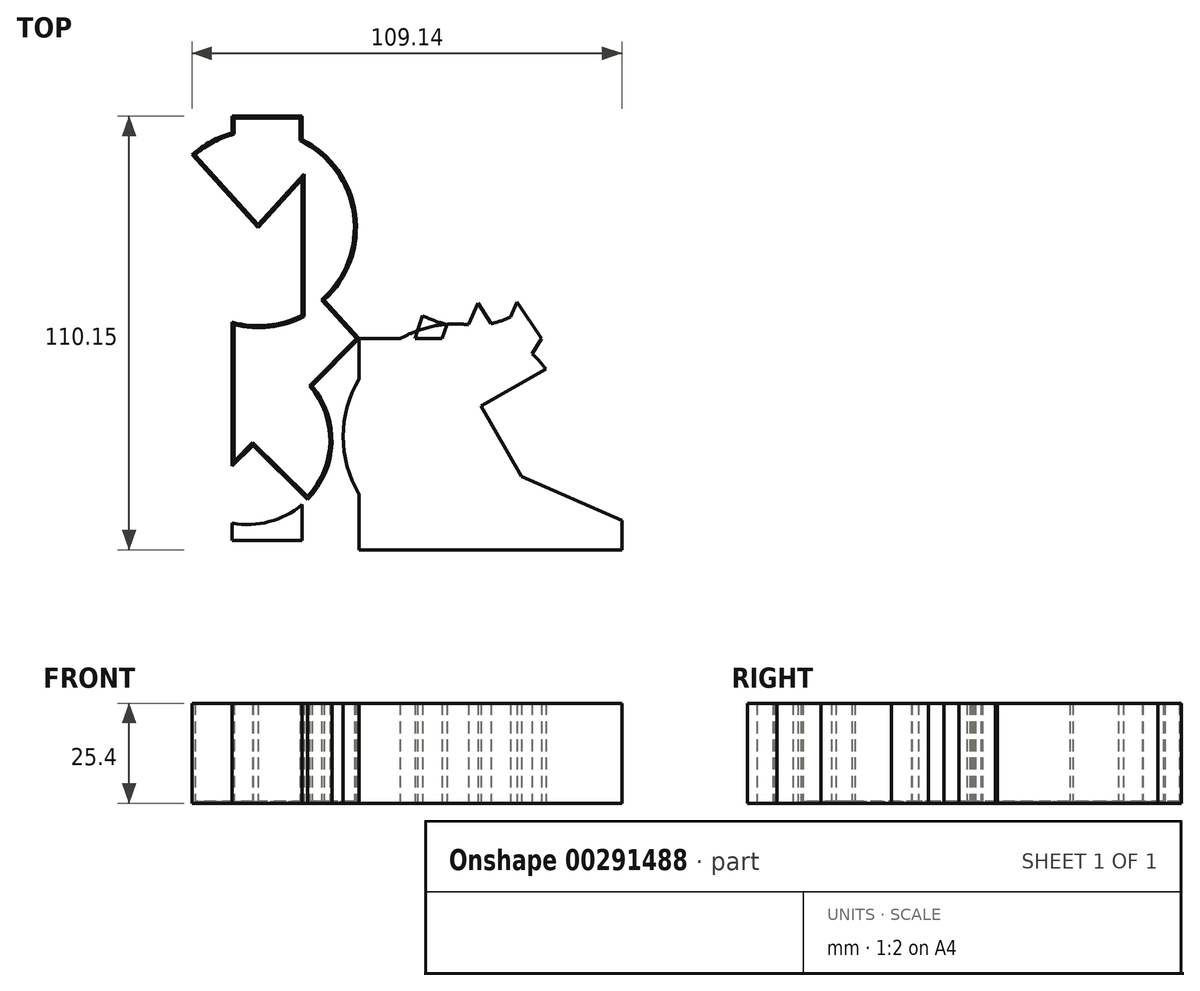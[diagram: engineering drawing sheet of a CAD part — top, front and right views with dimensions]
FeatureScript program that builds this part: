
annotation { "Feature Type Name" : "Feature", "Feature Type Description" : "" }
export const myFeature = defineFeature(function(context is Context, id is Id, definition is map)
    precondition{}
    {
        {
            var Q0;
            Q0=qCreatedBy(makeId("Top.planeOp"),FACE);
            var sketch = newSketch(context, id + "F0", { "sketchPlane" : qUnion([Q0])});
            skLineSegment(sketch, "E0.bottom", {"start": v(-41.08, 59.73) * mm, "end": v(-23.36, 59.73) * mm});
            skLineSegment(sketch, "E0.left", {"start": v(-60.14, 3.2) * mm, "end": v(-60.14, 0) * mm});
            skLineSegment(sketch, "E0.right", {"start": v(-8.86, 4.62) * mm, "end": v(-8.86, 3.2) * mm});
            skLineSegment(sketch, "E1.top", {"start": v(-60.14, 3.2) * mm, "end": v(-23.36, 3.2) * mm});
            skLineSegment(sketch, "E2", {"start": v(27.12, 3.2) * mm, "end": v(27.12, 3.2) * mm});
            skLineSegment(sketch, "E3.top", {"start": v(-41.08, -48.07) * mm, "end": v(-23.36, -48.07) * mm});
            skLineSegment(sketch, "E3.left", {"start": v(-41.08, 59.73) * mm, "end": v(-41.08, 55.54) * mm});
            skLineSegment(sketch, "E3.right", {"start": v(-23.36, 59.73) * mm, "end": v(-23.36, -48.07) * mm});
            skLineSegment(sketch, "E4", {"start": v(-51.27, 49.95) * mm, "end": v(-34.5, 31.47) * mm});
            skPoint(sketch, "E4.endSnap0", {"position": v(-8.86, 4.62) * mm});
            skLineSegment(sketch, "E5", {"start": v(-8.86, 3.2) * mm, "end": v(-23.36, -11.36) * mm});
            skLineSegment(sketch, "E6", {"start": v(-8.86, 59.73) * mm, "end": v(-34.5, 31.47) * mm});
            skArc(sketch, "E7", {"start": v(-51.27, 13) * mm, "mid": v(-9.55, 31.47) * mm, "end": v(-51.27, 49.95) * mm});
            skPoint(sketch, "E8.centerSnap0", {"position": v(-34.5, -25.24) * mm});
            skPoint(sketch, "E9.centerSnap0", {"position": v(-34.5, -22.56) * mm});
            skLineSegment(sketch, "E10.bottom", {"start": v(-8.86, 3.2) * mm, "end": v(17.29, 3.2) * mm});
            skLineSegment(sketch, "E10.top", {"start": v(-8.86, -50.42) * mm, "end": v(57.87, -50.42) * mm});
            skLineSegment(sketch, "E10.left", {"start": v(-8.86, 3.2) * mm, "end": v(-8.86, -50.42) * mm});
            skLineSegment(sketch, "E10.right", {"start": v(57.87, -43.02) * mm, "end": v(57.87, -50.42) * mm});
            skArc(sketch, "E11", {"start": v(5.39, -48.37) * mm, "mid": v(12.64, -50.13) * mm, "end": v(20.1, -49.96) * mm});
            skLineSegment(sketch, "E12", {"start": v(22.08, -13.94) * mm, "end": v(43.06, -50.42) * mm});
            skLineSegment(sketch, "E13", {"start": v(37.5, 3.2) * mm, "end": v(29.47, -9.69) * mm});
            skLineSegment(sketch, "E14", {"start": v(-11.46, -12.65) * mm, "end": v(-8.86, -13.79) * mm});
            skLineSegment(sketch, "E15", {"start": v(42.4, 0) * mm, "end": v(44.2, -18.96) * mm});
            skLineSegment(sketch, "E16", {"start": v(51.9, 3.2) * mm, "end": v(22.08, -13.94) * mm});
            skLineSegment(sketch, "E17", {"start": v(11.77, -19.86) * mm, "end": v(20.1, -49.96) * mm});
            skLineSegment(sketch, "E18.trimOffspring", {"start": v(13.5, 6.86) * mm, "end": v(12.22, 3.2) * mm});
            skLineSegment(sketch, "E19.trimOffspring", {"start": v(7.23, 9.08) * mm, "end": v(5.39, 3.2) * mm});
            skLineSegment(sketch, "E20.trimOffspring", {"start": v(-34.5, -22.56) * mm, "end": v(-41.08, -29.17) * mm});
            skLineSegment(sketch, "E21.trimOffspring", {"start": v(27.12, 3.2) * mm, "end": v(56.48, 3.2) * mm});
            skLineSegment(sketch, "E22.trimOffspring", {"start": v(-23.36, 19.19) * mm, "end": v(-8.86, 3.2) * mm});
            skArc(sketch, "E23.trimOffspring", {"start": v(27.63, 4.35) * mm, "mid": v(14.46, 6.92) * mm, "end": v(1.56, 3.2) * mm});
            skLineSegment(sketch, "E24.trimOffspring", {"start": v(-41.08, 38.72) * mm, "end": v(-41.08, -48.07) * mm});
            skLineSegment(sketch, "E25.trimOffspring", {"start": v(8.85, -21.54) * mm, "end": v(57.87, -43.02) * mm});
            skLineSegment(sketch, "E26.trimOffspring", {"start": v(19.25, -26.1) * mm, "end": v(5.39, -48.37) * mm});
            skArc(sketch, "E27.trimOffspring", {"start": v(38.57, -4.45) * mm, "mid": v(34.6, -0.18) * mm, "end": v(29.85, 3.2) * mm});
            skPoint(sketch, "E28.orphan", {"position": v(17.29, 3.2) * mm});
            skLineSegment(sketch, "E29.trimOffspring", {"start": v(25.47, 21.33) * mm, "end": v(18.68, 6.3) * mm});
            skLineSegment(sketch, "E30.trimOffspring", {"start": v(-8.86, 3.2) * mm, "end": v(12.22, 3.2) * mm});
            skLineSegment(sketch, "E31.trimOffspring", {"start": v(-51.27, 13) * mm, "end": v(-60.14, 3.2) * mm});
            skArc(sketch, "E32.trimOffspring", {"start": v(7.23, 9.08) * mm, "mid": v(20.14, 6.33) * mm, "end": v(32.67, 10.49) * mm});
            skPoint(sketch, "E33.orphan", {"position": v(-60.14, -48.33) * mm});
            skArc(sketch, "E34.trimOffspring", {"start": v(-41.08, -43.67) * mm, "mid": v(-17.83, -31.73) * mm, "end": v(-23.36, -6.2) * mm});
            skLineSegment(sketch, "E35.trimOffspring", {"start": v(-8.86, -6.98) * mm, "end": v(-8.86, -50.49) * mm});
            skArc(sketch, "E36.trimOffspring", {"start": v(-8.86, -6.98) * mm, "mid": v(-12.92, -21.67) * mm, "end": v(-8.86, -36.36) * mm});
            skLineSegment(sketch, "E37.trimOffspring", {"start": v(21.37, 12.25) * mm, "end": v(27.12, 3.2) * mm});
            skLineSegment(sketch, "E38.trimOffspring", {"start": v(-41.08, -18.77) * mm, "end": v(-8.86, -50.49) * mm});
            skLineSegment(sketch, "E39.trimOffspring", {"start": v(11.77, -19.86) * mm, "end": v(-8.86, -31.73) * mm});
            skLineSegment(sketch, "E40.trimOffspring", {"start": v(31.32, 12.51) * mm, "end": v(27.12, 3.2) * mm});
            skPoint(sketch, "E41.trimOffspring.end.orphan", {"position": v(0, 59.73) * mm});
            skLineSegment(sketch, "E42.trimOffspring", {"start": v(31.32, 12.51) * mm, "end": v(37.5, 3.2) * mm});
            skLineSegment(sketch, "E43.trimOffspring", {"start": v(27.12, 3.2) * mm, "end": v(57.87, 3.2) * mm});
            skLineSegment(sketch, "E44.trimOffspring", {"start": v(46, -37.82) * mm, "end": v(47.2, -50.42) * mm});
            skArc(sketch, "E45.trimOffspring", {"start": v(37.32, -40.44) * mm, "mid": v(39.17, -38.07) * mm, "end": v(40.76, -35.52) * mm});
            skSolve(sketch);
        }
        {
            var Q0;
            {var subQ1=sQuery(id+"F0.wireOp",EDGE,"E11");Q0=makeQuery(id+"F0.imprint","IMPRINT",FACE,{"disambiguationData":[TD([[makeQuery(id+"F0.imprint","IMPRINT",EDGE,{"derivedFrom":subQ1}),-1.0]])]});}
            var Q1;
            {var subQ0=sQuery(id+"F0.wireOp",EDGE,"E22.trimOffspring");var subQ1=sQuery(id+"F0.wireOp",EDGE,"E3.right");var subQ2=makeQuery(id+"F0.imprint","INTERSECT",VERTEX,{"derivedFrom":[subQ1,subQ0]});Q1=makeQuery(id+"F0.imprint","IMPRINT",FACE,{"disambiguationData":[TD([[makeQuery(id+"F0.imprint","IMPRINT",EDGE,{"disambiguationData":[TD([[subQ2,-1.0]])],"derivedFrom":subQ1}),1.0]])]});}
            var Q2;
            {var subQ0=sQuery(id+"F0.wireOp",EDGE,"E22.trimOffspring");var subQ1=sQuery(id+"F0.wireOp",EDGE,"E3.right");var subQ2=makeQuery(id+"F0.imprint","INTERSECT",VERTEX,{"derivedFrom":[subQ1,subQ0]});Q2=makeQuery(id+"F0.imprint","IMPRINT",FACE,{"disambiguationData":[TD([[makeQuery(id+"F0.imprint","IMPRINT",EDGE,{"disambiguationData":[TD([[subQ2,1.0]])],"derivedFrom":subQ1}),1.0]])]});}
            var Q3;
            {var subQ3=sQuery(id+"F0.wireOp",EDGE,"E3.right");var subQ5=sQuery(id+"F0.wireOp",EDGE,"E7");var subQ9=makeQuery(id+"F0.imprint","INTERSECT",VERTEX,{"disambiguationData":[OD(0.0)],"derivedFrom":[subQ3,subQ5]});Q3=makeQuery(id+"F0.imprint","IMPRINT",FACE,{"disambiguationData":[TD([[makeQuery(id+"F0.imprint","IMPRINT",EDGE,{"disambiguationData":[TD([[subQ9,-1.0]])],"derivedFrom":subQ3}),-1.0]])]});}
            var Q4;
            {var subQ3=sQuery(id+"F0.wireOp",EDGE,"E3.right");var subQ9=makeQuery(id+"F0.imprint","INTERSECT",VERTEX,{"derivedFrom":[sQuery(id+"F0.wireOp",EDGE,"E1.top"),subQ3]});Q4=makeQuery(id+"F0.imprint","IMPRINT",FACE,{"disambiguationData":[TD([[makeQuery(id+"F0.imprint","IMPRINT",EDGE,{"disambiguationData":[TD([[subQ9,1.0]])],"derivedFrom":subQ3}),1.0]])]});}
            var Q5;
            {var subQ15=sQuery(id+"F0.wireOp",EDGE,"E10.left");Q5=makeQuery(id+"F0.imprint","IMPRINT",FACE,{"disambiguationData":[TD([[makeQuery(id+"F0.imprint","IMPRINT",EDGE,{"derivedFrom":subQ15}),1.0]])]});}
            var Q6;
            {var subQ0=sQuery(id+"F0.wireOp",EDGE,"E44.trimOffspring");Q6=makeQuery(id+"F0.imprint","IMPRINT",FACE,{"disambiguationData":[TD([[makeQuery(id+"F0.imprint","IMPRINT",EDGE,{"derivedFrom":subQ0}),-1.0]])]});}
            var Q7;
            {var subQ0=sQuery(id+"F0.wireOp",EDGE,"E26.trimOffspring");var subQ1=sQuery(id+"F0.wireOp",EDGE,"E17");var subQ2=makeQuery(id+"F0.imprint","INTERSECT",VERTEX,{"derivedFrom":[subQ1,subQ0]});Q7=makeQuery(id+"F0.imprint","IMPRINT",FACE,{"disambiguationData":[TD([[makeQuery(id+"F0.imprint","IMPRINT",EDGE,{"disambiguationData":[TD([[subQ2,1.0]])],"derivedFrom":subQ1}),1.0]])]});}
            var Q8;
            {var subQ0=sQuery(id+"F0.wireOp",EDGE,"E24.trimOffspring");var subQ1=sQuery(id+"F0.wireOp",EDGE,"E20.trimOffspring");var subQ2=makeQuery(id+"F0.imprint","INTERSECT",VERTEX,{"derivedFrom":[subQ1,subQ0]});Q8=makeQuery(id+"F0.imprint","IMPRINT",FACE,{"disambiguationData":[TD([[makeQuery(id+"F0.imprint","IMPRINT",EDGE,{"disambiguationData":[TD([[subQ2,1.0]])],"derivedFrom":subQ1}),-1.0]])]});}
            var Q9;
            {var subQ0=sQuery(id+"F0.wireOp",EDGE,"E5");var subQ1=sQuery(id+"F0.wireOp",EDGE,"E3.right");var subQ2=makeQuery(id+"F0.imprint","INTERSECT",VERTEX,{"derivedFrom":[subQ1,subQ0]});Q9=makeQuery(id+"F0.imprint","IMPRINT",FACE,{"disambiguationData":[TD([[makeQuery(id+"F0.imprint","IMPRINT",EDGE,{"disambiguationData":[TD([[subQ2,-1.0]])],"derivedFrom":subQ1}),1.0]])]});}
            var Q10;
            {var subQ0=sQuery(id+"F0.wireOp",EDGE,"E14");Q10=makeQuery(id+"F0.imprint","IMPRINT",FACE,{"disambiguationData":[TD([[makeQuery(id+"F0.imprint","IMPRINT",EDGE,{"derivedFrom":subQ0}),-1.0]])]});}
            var Q11;
            {var subQ0=sQuery(id+"F0.wireOp",EDGE,"E0.bottom");Q11=makeQuery(id+"F0.imprint","IMPRINT",FACE,{"disambiguationData":[TD([[makeQuery(id+"F0.imprint","IMPRINT",EDGE,{"derivedFrom":subQ0}),-1.0]])]});}
            var Q12;
            {var subQ0=sQuery(id+"F0.wireOp",EDGE,"E40.trimOffspring");var subQ1=sQuery(id+"F0.wireOp",EDGE,"E23.trimOffspring");var subQ2=makeQuery(id+"F0.imprint","INTERSECT",VERTEX,{"derivedFrom":[subQ1,subQ0]});Q12=makeQuery(id+"F0.imprint","IMPRINT",FACE,{"disambiguationData":[TD([[makeQuery(id+"F0.imprint","IMPRINT",EDGE,{"disambiguationData":[TD([[subQ2,-1.0]])],"derivedFrom":subQ1}),-1.0]])]});}
            var Q13;
            {var subQ0=sQuery(id+"F0.wireOp",EDGE,"E3.top");Q13=makeQuery(id+"F0.imprint","IMPRINT",FACE,{"disambiguationData":[TD([[makeQuery(id+"F0.imprint","IMPRINT",EDGE,{"derivedFrom":subQ0}),1.0]])]});}
            var Q14;
            {var subQ0=sQuery(id+"F0.wireOp",EDGE,"E10.right");Q14=makeQuery(id+"F0.imprint","IMPRINT",FACE,{"disambiguationData":[TD([[makeQuery(id+"F0.imprint","IMPRINT",EDGE,{"derivedFrom":subQ0}),-1.0]])]});}
            var Q15;
            {var subQ0=sQuery(id+"F0.wireOp",EDGE,"E11");Q15=makeQuery(id+"F0.imprint","IMPRINT",FACE,{"disambiguationData":[TD([[makeQuery(id+"F0.imprint","IMPRINT",EDGE,{"derivedFrom":subQ0}),1.0]])]});}
            var Q16;
            {var subQ0=sQuery(id+"F0.wireOp",EDGE,"E5");var subQ1=sQuery(id+"F0.wireOp",EDGE,"E3.right");var subQ2=makeQuery(id+"F0.imprint","INTERSECT",VERTEX,{"derivedFrom":[subQ1,subQ0]});Q16=makeQuery(id+"F0.imprint","IMPRINT",FACE,{"disambiguationData":[TD([[makeQuery(id+"F0.imprint","IMPRINT",EDGE,{"disambiguationData":[TD([[subQ2,1.0]])],"derivedFrom":subQ1}),1.0]])]});}
            var Q17;
            {var subQ4=sQuery(id+"F0.wireOp",EDGE,"E32.trimOffspring");var subQ6=sQuery(id+"F0.wireOp",EDGE,"E42.trimOffspring");var subQ7=makeQuery(id+"F0.imprint","INTERSECT",VERTEX,{"derivedFrom":[subQ4,subQ6]});Q17=makeQuery(id+"F0.imprint","IMPRINT",FACE,{"disambiguationData":[TD([[makeQuery(id+"F0.imprint","IMPRINT",EDGE,{"disambiguationData":[TD([[subQ7,1.0]])],"derivedFrom":subQ4}),-1.0]])]});}
            var Q18;
            {var subQ0=sQuery(id+"F0.wireOp",EDGE,"E32.trimOffspring");var subQ1=sQuery(id+"F0.wireOp",EDGE,"E19.trimOffspring");var subQ2=makeQuery(id+"F0.imprint","INTERSECT",VERTEX,{"derivedFrom":[subQ1,subQ0]});Q18=makeQuery(id+"F0.imprint","IMPRINT",FACE,{"disambiguationData":[TD([[makeQuery(id+"F0.imprint","IMPRINT",EDGE,{"disambiguationData":[TD([[subQ2,-1.0]])],"derivedFrom":subQ1}),1.0]])]});}
            var Q19;
            {var subQ0=sQuery(id+"F0.wireOp",EDGE,"E3.right");var subQ1=sQuery(id+"F0.wireOp",EDGE,"E1.top");var subQ2=makeQuery(id+"F0.imprint","INTERSECT",VERTEX,{"derivedFrom":[subQ1,subQ0]});Q19=makeQuery(id+"F0.imprint","IMPRINT",FACE,{"disambiguationData":[TD([[makeQuery(id+"F0.imprint","IMPRINT",EDGE,{"disambiguationData":[TD([[subQ2,1.0]])],"derivedFrom":subQ1}),1.0]])]});}
            var Q20;
            {var subQ0=sQuery(id+"F0.wireOp",EDGE,"E7");var subQ1=sQuery(id+"F0.wireOp",EDGE,"E3.right");var subQ2=makeQuery(id+"F0.imprint","INTERSECT",VERTEX,{"disambiguationData":[OD(0.0)],"derivedFrom":[subQ1,subQ0]});Q20=makeQuery(id+"F0.imprint","IMPRINT",FACE,{"disambiguationData":[TD([[makeQuery(id+"F0.imprint","IMPRINT",EDGE,{"disambiguationData":[TD([[subQ2,-1.0]])],"derivedFrom":subQ1}),1.0]])]});}
            var Q21;
            {var subQ0=sQuery(id+"F0.wireOp",EDGE,"E45.trimOffspring");Q21=makeQuery(id+"F0.imprint","IMPRINT",FACE,{"disambiguationData":[TD([[makeQuery(id+"F0.imprint","IMPRINT",EDGE,{"derivedFrom":subQ0}),1.0]])]});}
            var Q22;
            {var subQ0=sQuery(id+"F0.wireOp",EDGE,"E43.trimOffspring");var subQ5=sQuery(id+"F0.wireOp",EDGE,"E16");var subQ6=makeQuery(id+"F0.imprint","INTERSECT",VERTEX,{"derivedFrom":[subQ5,subQ0]});Q22=makeQuery(id+"F0.imprint","IMPRINT",FACE,{"disambiguationData":[TD([[makeQuery(id+"F0.imprint","IMPRINT",EDGE,{"disambiguationData":[TD([[subQ6,-1.0]])],"derivedFrom":subQ5}),-1.0]])]});}
            var Q23;
            {var subQ0=sQuery(id+"F0.wireOp",EDGE,"E16");var subQ1=sQuery(id+"F0.wireOp",EDGE,"E13");var subQ2=makeQuery(id+"F0.imprint","INTERSECT",VERTEX,{"derivedFrom":[subQ1,subQ0]});Q23=makeQuery(id+"F0.imprint","IMPRINT",FACE,{"disambiguationData":[TD([[makeQuery(id+"F0.imprint","IMPRINT",EDGE,{"disambiguationData":[TD([[subQ2,1.0]])],"derivedFrom":subQ1}),1.0]])]});}
            var Q24;
            {var subQ9=sQuery(id+"F0.wireOp",EDGE,"E10.left");Q24=makeQuery(id+"F0.imprint","IMPRINT",FACE,{"disambiguationData":[TD([[makeQuery(id+"F0.imprint","IMPRINT",EDGE,{"derivedFrom":subQ9}),-1.0]])]});}
            var Q25;
            {var subQ0=sQuery(id+"F0.wireOp",EDGE,"E43.trimOffspring");var subQ3=sQuery(id+"F0.wireOp",EDGE,"E27.trimOffspring");var subQ5=makeQuery(id+"F0.imprint","INTERSECT",VERTEX,{"derivedFrom":[subQ3,subQ0]});Q25=makeQuery(id+"F0.imprint","IMPRINT",FACE,{"disambiguationData":[TD([[makeQuery(id+"F0.imprint","IMPRINT",EDGE,{"disambiguationData":[TD([[subQ5,1.0]])],"derivedFrom":subQ3}),-1.0]])]});}
            var Q26;
            {var subQ0=sQuery(id+"F0.wireOp",EDGE,"E30.trimOffspring");var subQ1=sQuery(id+"F0.wireOp",EDGE,"E18.trimOffspring");var subQ2=makeQuery(id+"F0.imprint","INTERSECT",VERTEX,{"derivedFrom":[subQ1,subQ0]});Q26=makeQuery(id+"F0.imprint","IMPRINT",FACE,{"disambiguationData":[TD([[makeQuery(id+"F0.imprint","IMPRINT",EDGE,{"disambiguationData":[TD([[subQ2,1.0]])],"derivedFrom":subQ1}),-1.0]])]});}
            var Q27;
            {var subQ0=sQuery(id+"F0.wireOp",EDGE,"E29.trimOffspring");var subQ1=sQuery(id+"F0.wireOp",EDGE,"E23.trimOffspring");var subQ2=makeQuery(id+"F0.imprint","INTERSECT",VERTEX,{"derivedFrom":[subQ1,subQ0]});Q27=makeQuery(id+"F0.imprint","IMPRINT",FACE,{"disambiguationData":[TD([[makeQuery(id+"F0.imprint","IMPRINT",EDGE,{"disambiguationData":[TD([[subQ2,1.0]])],"derivedFrom":subQ1}),-1.0]])]});}
            var Q28;
            {var subQ0=sQuery(id+"F0.wireOp",EDGE,"E34.trimOffspring");var subQ3=sQuery(id+"F0.wireOp",EDGE,"E3.right");var subQ4=makeQuery(id+"F0.imprint","INTERSECT",VERTEX,{"disambiguationData":[OD(1.0)],"derivedFrom":[subQ3,subQ0]});Q28=makeQuery(id+"F0.imprint","IMPRINT",FACE,{"disambiguationData":[TD([[makeQuery(id+"F0.imprint","IMPRINT",EDGE,{"disambiguationData":[TD([[subQ4,1.0]])],"derivedFrom":subQ3}),-1.0]])]});}
            var Q29;
            {var subQ0=sQuery(id+"F0.wireOp",EDGE,"E29.trimOffspring");var subQ1=sQuery(id+"F0.wireOp",EDGE,"E23.trimOffspring");var subQ2=makeQuery(id+"F0.imprint","INTERSECT",VERTEX,{"derivedFrom":[subQ1,subQ0]});Q29=makeQuery(id+"F0.imprint","IMPRINT",FACE,{"disambiguationData":[TD([[makeQuery(id+"F0.imprint","IMPRINT",EDGE,{"disambiguationData":[TD([[subQ2,1.0]])],"derivedFrom":subQ1}),1.0]])]});}
            var Q30;
            {var subQ0=sQuery(id+"F0.wireOp",EDGE,"E30.trimOffspring");var subQ1=sQuery(id+"F0.wireOp",EDGE,"E19.trimOffspring");var subQ2=makeQuery(id+"F0.imprint","INTERSECT",VERTEX,{"derivedFrom":[subQ1,subQ0]});Q30=makeQuery(id+"F0.imprint","IMPRINT",FACE,{"disambiguationData":[TD([[makeQuery(id+"F0.imprint","IMPRINT",EDGE,{"disambiguationData":[TD([[subQ2,1.0]])],"derivedFrom":subQ1}),-1.0]])]});}
            var Q31;
            {var subQ0=sQuery(id+"F0.wireOp",EDGE,"E23.trimOffspring");var subQ1=sQuery(id+"F0.wireOp",EDGE,"E18.trimOffspring");var subQ2=makeQuery(id+"F0.imprint","INTERSECT",VERTEX,{"derivedFrom":[subQ1,subQ0]});Q31=makeQuery(id+"F0.imprint","IMPRINT",FACE,{"disambiguationData":[TD([[makeQuery(id+"F0.imprint","IMPRINT",EDGE,{"disambiguationData":[TD([[subQ2,-1.0]])],"derivedFrom":subQ1}),1.0]])]});}
            var Q32;
            {var subQ0=sQuery(id+"F0.wireOp",EDGE,"E14");Q32=makeQuery(id+"F0.imprint","IMPRINT",FACE,{"disambiguationData":[TD([[makeQuery(id+"F0.imprint","IMPRINT",EDGE,{"derivedFrom":subQ0}),1.0]])]});}
            var Q33;
            {var subQ0=sQuery(id+"F0.wireOp",EDGE,"E42.trimOffspring");var subQ1=sQuery(id+"F0.wireOp",EDGE,"E32.trimOffspring");var subQ2=makeQuery(id+"F0.imprint","INTERSECT",VERTEX,{"derivedFrom":[subQ1,subQ0]});Q33=makeQuery(id+"F0.imprint","IMPRINT",FACE,{"disambiguationData":[TD([[makeQuery(id+"F0.imprint","IMPRINT",EDGE,{"disambiguationData":[TD([[subQ2,1.0]])],"derivedFrom":subQ1}),1.0]])]});}
            var Q34;
            {var subQ0=sQuery(id+"F0.wireOp",EDGE,"E34.trimOffspring");var subQ1=sQuery(id+"F0.wireOp",EDGE,"E3.right");var subQ2=makeQuery(id+"F0.imprint","INTERSECT",VERTEX,{"disambiguationData":[OD(1.0)],"derivedFrom":[subQ1,subQ0]});Q34=makeQuery(id+"F0.imprint","IMPRINT",FACE,{"disambiguationData":[TD([[makeQuery(id+"F0.imprint","IMPRINT",EDGE,{"disambiguationData":[TD([[subQ2,1.0]])],"derivedFrom":subQ1}),1.0]])]});}
            var Q35;
            {var subQ0=sQuery(id+"F0.wireOp",EDGE,"E39.trimOffspring");var subQ1=sQuery(id+"F0.wireOp",EDGE,"E17");var subQ2=makeQuery(id+"F0.imprint","INTERSECT",VERTEX,{"derivedFrom":[subQ1,subQ0]});Q35=makeQuery(id+"F0.imprint","IMPRINT",FACE,{"disambiguationData":[TD([[makeQuery(id+"F0.imprint","IMPRINT",EDGE,{"disambiguationData":[TD([[subQ2,-1.0]])],"derivedFrom":subQ1}),-1.0]])]});}
            var Q36;
            {var subQ0=sQuery(id+"F0.wireOp",EDGE,"E37.trimOffspring");var subQ1=sQuery(id+"F0.wireOp",EDGE,"E23.trimOffspring");var subQ2=makeQuery(id+"F0.imprint","INTERSECT",VERTEX,{"derivedFrom":[subQ1,subQ0]});Q36=makeQuery(id+"F0.imprint","IMPRINT",FACE,{"disambiguationData":[TD([[makeQuery(id+"F0.imprint","IMPRINT",EDGE,{"disambiguationData":[TD([[subQ2,-1.0]])],"derivedFrom":subQ1}),-1.0]])]});}
            var Q37;
            {var subQ0=sQuery(id+"F0.wireOp",EDGE,"E23.trimOffspring");var subQ1=sQuery(id+"F0.wireOp",EDGE,"E18.trimOffspring");var subQ2=makeQuery(id+"F0.imprint","INTERSECT",VERTEX,{"derivedFrom":[subQ1,subQ0]});Q37=makeQuery(id+"F0.imprint","IMPRINT",FACE,{"disambiguationData":[TD([[makeQuery(id+"F0.imprint","IMPRINT",EDGE,{"disambiguationData":[TD([[subQ2,-1.0]])],"derivedFrom":subQ1}),-1.0]])]});}
            var Q38;
            {var subQ0=sQuery(id+"F0.wireOp",EDGE,"E40.trimOffspring");var subQ1=sQuery(id+"F0.wireOp",EDGE,"E23.trimOffspring");var subQ2=makeQuery(id+"F0.imprint","INTERSECT",VERTEX,{"derivedFrom":[subQ1,subQ0]});Q38=makeQuery(id+"F0.imprint","IMPRINT",FACE,{"disambiguationData":[TD([[makeQuery(id+"F0.imprint","IMPRINT",EDGE,{"disambiguationData":[TD([[subQ2,-1.0]])],"derivedFrom":subQ1}),1.0]])]});}
            var Q39;
            {var subQ0=sQuery(id+"F0.wireOp",EDGE,"E3.right");var subQ3=sQuery(id+"F0.wireOp",EDGE,"E1.top");var subQ4=makeQuery(id+"F0.imprint","INTERSECT",VERTEX,{"derivedFrom":[subQ3,subQ0]});Q39=makeQuery(id+"F0.imprint","IMPRINT",FACE,{"disambiguationData":[TD([[makeQuery(id+"F0.imprint","IMPRINT",EDGE,{"disambiguationData":[TD([[subQ4,1.0]])],"derivedFrom":subQ3}),-1.0]])]});}
            extrude(context, id + "F1", {"entities" : qUnion([Q0, Q1, Q2, Q3, Q4, Q5, Q6, Q7, Q8, Q9, Q10, Q11, Q12, Q13, Q14, Q15, Q16, Q17, Q18, Q19, Q20, Q21, Q22, Q23, Q24, Q25, Q26, Q27, Q28, Q29, Q30, Q31, Q32, Q33, Q34, Q35, Q36, Q37, Q38, Q39]), "depth" : 25.4 * mm});
        }
        {
            var Q0;
            Q0=makeQuery(id+"F1.opExtrude","CAP_FACE",FACE,{"disambiguationData":[OSD([sQuery(id+"F0.wireOp",EDGE,"E0.bottom"),sQuery(id+"F0.wireOp",EDGE,"E3.top"),sQuery(id+"F0.wireOp",EDGE,"E3.left"),sQuery(id+"F0.wireOp",EDGE,"E3.right"),sQuery(id+"F0.wireOp",EDGE,"E4"),sQuery(id+"F0.wireOp",EDGE,"E6"),sQuery(id+"F0.wireOp",EDGE,"E7"),sQuery(id+"F0.wireOp",EDGE,"E10.top"),sQuery(id+"F0.wireOp",EDGE,"E10.right"),sQuery(id+"F0.wireOp",EDGE,"E12"),sQuery(id+"F0.wireOp",EDGE,"E16"),sQuery(id+"F0.wireOp",EDGE,"E19.trimOffspring"),sQuery(id+"F0.wireOp",EDGE,"E22.trimOffspring"),sQuery(id+"F0.wireOp",EDGE,"E23.trimOffspring"),sQuery(id+"F0.wireOp",EDGE,"E24.trimOffspring"),sQuery(id+"F0.wireOp",EDGE,"E25.trimOffspring"),sQuery(id+"F0.wireOp",EDGE,"E29.trimOffspring"),sQuery(id+"F0.wireOp",EDGE,"E30.trimOffspring"),sQuery(id+"F0.wireOp",EDGE,"E32.trimOffspring"),sQuery(id+"F0.wireOp",EDGE,"E34.trimOffspring"),sQuery(id+"F0.wireOp",EDGE,"E35.trimOffspring"),sQuery(id+"F0.wireOp",EDGE,"E37.trimOffspring"),sQuery(id+"F0.wireOp",EDGE,"E38.trimOffspring"),sQuery(id+"F0.wireOp",EDGE,"E40.trimOffspring"),sQuery(id+"F0.wireOp",EDGE,"E42.trimOffspring"),sQuery(id+"F0.wireOp",EDGE,"E43.trimOffspring")])],"isStart":false});
            shell(context, id + "F2", {"entities" : qUnion([Q0]), "thickness" : 0.5 * mm});
        }
    });
